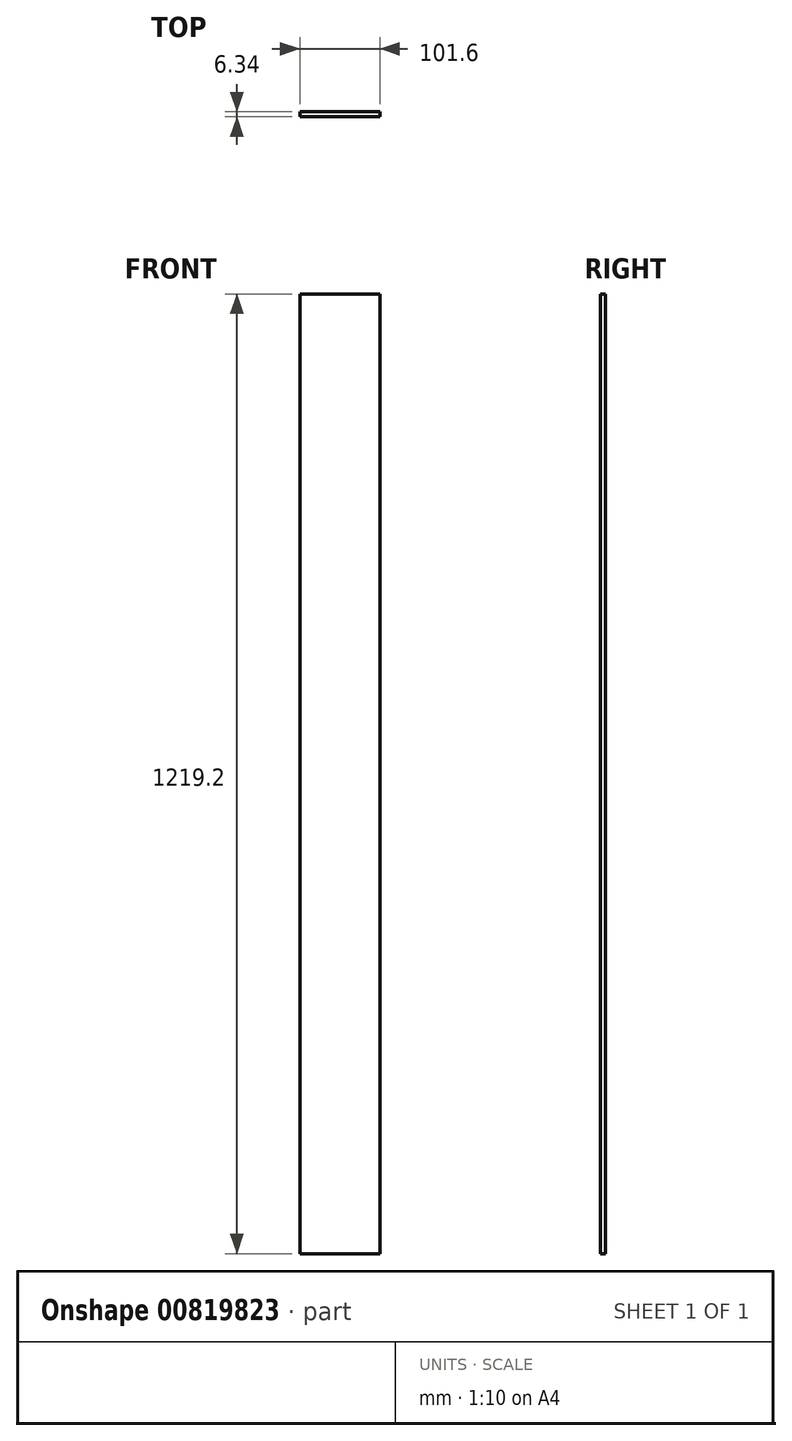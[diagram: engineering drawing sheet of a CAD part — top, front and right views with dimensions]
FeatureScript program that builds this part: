
annotation { "Feature Type Name" : "Feature", "Feature Type Description" : "" }
export const myFeature = defineFeature(function(context is Context, id is Id, definition is map)
    precondition{}
    {
        {
            var Q0;
            Q0=qCreatedBy(makeId("Top.planeOp"),FACE);
            var sketch = newSketch(context, id + "F0", { "sketchPlane" : qUnion([Q0])});
            skLineSegment(sketch, "E0.bottom", {"start": v(50.8, 3.18) * mm, "end": v(-50.8, 3.18) * mm});
            skLineSegment(sketch, "E0.top", {"start": v(50.8, -3.17) * mm, "end": v(-50.8, -3.17) * mm});
            skLineSegment(sketch, "E0.left", {"start": v(50.8, 3.18) * mm, "end": v(50.8, -3.17) * mm});
            skLineSegment(sketch, "E0.right", {"start": v(-50.8, 3.18) * mm, "end": v(-50.8, -3.17) * mm});
            skPoint(sketch, "E0.middle", {"position": v(0, 0) * mm});
            skSolve(sketch);
        }
        {
            var Q0;
            Q0 = qSketchRegion(id + "F0", true);
            extrude(context, id + "F1", {"entities" : qUnion([Q0]), "depth" : 1219.2 * mm, "offsetDistance" : 25.4 * mm});
        }
    });
